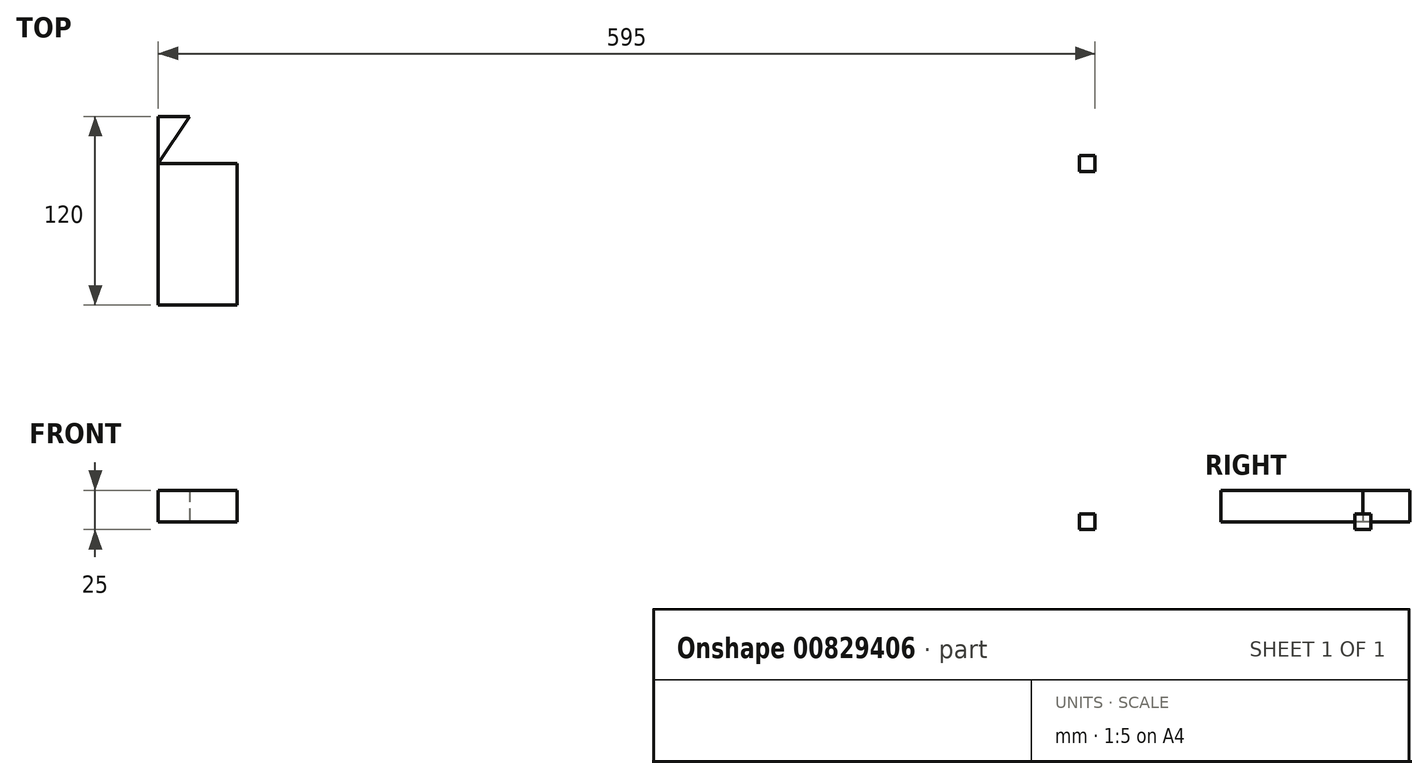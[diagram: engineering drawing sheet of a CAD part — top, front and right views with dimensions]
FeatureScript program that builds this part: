
annotation { "Feature Type Name" : "Feature", "Feature Type Description" : "" }
export const myFeature = defineFeature(function(context is Context, id is Id, definition is map)
    precondition{}
    {
        {
            var Q0;
            Q0=qCreatedBy(makeId("Top.planeOp"),FACE);
            var sketch = newSketch(context, id + "F0", { "sketchPlane" : qUnion([Q0])});
            skLineSegment(sketch, "E0.bottom", {"start": v(0, 0) * mm, "end": v(50, 0) * mm});
            skLineSegment(sketch, "E0.top", {"start": v(0, -120) * mm, "end": v(50, -120) * mm});
            skLineSegment(sketch, "E0.left", {"start": v(0, 0) * mm, "end": v(0, -120) * mm});
            skLineSegment(sketch, "E0.right", {"start": v(50, 0) * mm, "end": v(50, -120) * mm});
            skLineSegment(sketch, "E1", {"start": v(0, 0) * mm, "end": v(20, 0) * mm});
            skLineSegment(sketch, "E2", {"start": v(0, 0) * mm, "end": v(0, -30) * mm});
            skLineSegment(sketch, "E3", {"start": v(20, 0) * mm, "end": v(0, -30) * mm});
            skLineSegment(sketch, "E4", {"start": v(0, -30) * mm, "end": v(590, -30) * mm});
            skLineSegment(sketch, "E5.bottom", {"start": v(595, -35) * mm, "end": v(585, -35) * mm});
            skLineSegment(sketch, "E5.top", {"start": v(595, -25) * mm, "end": v(585, -25) * mm});
            skLineSegment(sketch, "E5.left", {"start": v(595, -35) * mm, "end": v(595, -25) * mm});
            skLineSegment(sketch, "E5.right", {"start": v(585, -35) * mm, "end": v(585, -25) * mm});
            skPoint(sketch, "E5.middle", {"position": v(590, -30) * mm});
            skSolve(sketch);
        }
        {
            var Q0;
            {var subQ0=sQuery(id+"F0.wireOp",EDGE,"E0.bottom");Q0=makeQuery(id+"F0.imprint","IMPRINT",FACE,{"disambiguationData":[TD([[makeQuery(id+"F0.imprint","IMPRINT",EDGE,{"derivedFrom":subQ0}),-1.0]])]});}
            var Q1;
            {var subQ0=sQuery(id+"F0.wireOp",EDGE,"E0.top");Q1=makeQuery(id+"F0.imprint","IMPRINT",FACE,{"disambiguationData":[TD([[makeQuery(id+"F0.imprint","IMPRINT",EDGE,{"derivedFrom":subQ0}),1.0]])]});}
            extrude(context, id + "F1", {"entities" : qUnion([Q0, Q1]), "depth" : 20 * mm, "offsetDistance" : 25 * mm});
        }
        {
            var Q0;
            {var subQ1=sQuery(id+"F0.wireOp",EDGE,"E5.bottom");Q0=makeQuery(id+"F0.imprint","IMPRINT",FACE,{"disambiguationData":[TD([[makeQuery(id+"F0.imprint","IMPRINT",EDGE,{"derivedFrom":subQ1}),-1.0]])]});}
            extrude(context, id + "F2", {"entities" : qUnion([Q0]), "endBound" : BoundingType.SYMMETRIC, "depth" : 10 * mm, "offsetDistance" : 25 * mm});
        }
    });
